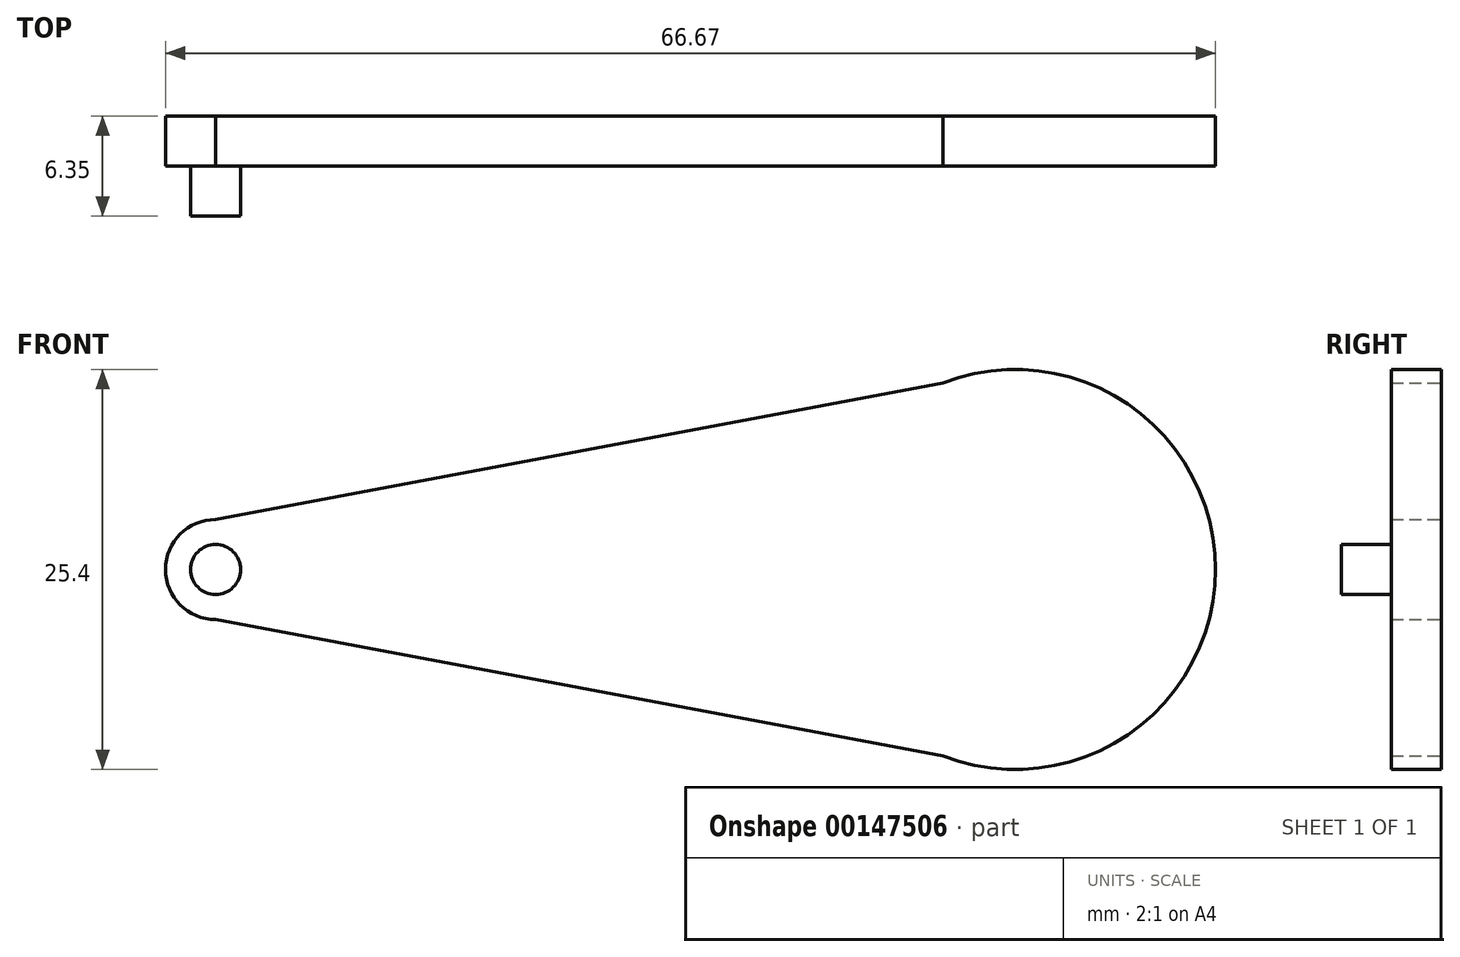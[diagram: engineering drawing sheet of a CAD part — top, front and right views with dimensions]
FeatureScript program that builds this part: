
annotation { "Feature Type Name" : "Feature", "Feature Type Description" : "" }
export const myFeature = defineFeature(function(context is Context, id is Id, definition is map)
    precondition{}
    {
        {
            var Q0;
            Q0=qCreatedBy(makeId("Front.planeOp"),FACE);
            var sketch = newSketch(context, id + "F0", { "sketchPlane" : qUnion([Q0])});
            skArc(sketch, "E0", {"start": v(-4.6, -11.84) * mm, "mid": v(12.7, 0) * mm, "end": v(-4.6, 11.84) * mm});
            skArc(sketch, "E1", {"start": v(-50.8, 3.18) * mm, "mid": v(-53.98, 0) * mm, "end": v(-50.8, -3.18) * mm});
            skLineSegment(sketch, "E2", {"start": v(-50.8, 3.17) * mm, "end": v(-4.6, 11.84) * mm});
            skLineSegment(sketch, "E3", {"start": v(-50.8, -3.17) * mm, "end": v(-4.6, -11.84) * mm});
            skPoint(sketch, "E4.orphan", {"position": v(0, -12.7) * mm});
            skPoint(sketch, "E5.orphan", {"position": v(0, 12.7) * mm});
            skSolve(sketch);
        }
        {
            var Q0;
            Q0 = qSketchRegion(id + "F0", true);
            extrude(context, id + "F1", {"entities" : qUnion([Q0]), "depth" : 3.17 * mm});
        }
        {
            var Q0;
            Q0=makeQuery(id+"F1.opExtrude","CAP_FACE",FACE,{"disambiguationData":[OSD([sQuery(id+"F0.wireOp",EDGE,"E0"),sQuery(id+"F0.wireOp",EDGE,"E1"),sQuery(id+"F0.wireOp",EDGE,"E2"),sQuery(id+"F0.wireOp",EDGE,"E3")])],"isStart":false});
            var sketch = newSketch(context, id + "F2", { "sketchPlane" : qUnion([Q0])});
            skCircle(sketch, "E6", {"center": v(-50.8, 0) * mm, "radius": 1.59 * mm});
            skSolve(sketch);
        }
        {
            var Q0;
            Q0 = qSketchRegion(id + "F2", true);
            extrude(context, id + "F3", {"entities" : qUnion([Q0]), "operationType" : NewBodyOperationType.ADD, "depth" : 3.17 * mm});
        }
    });
